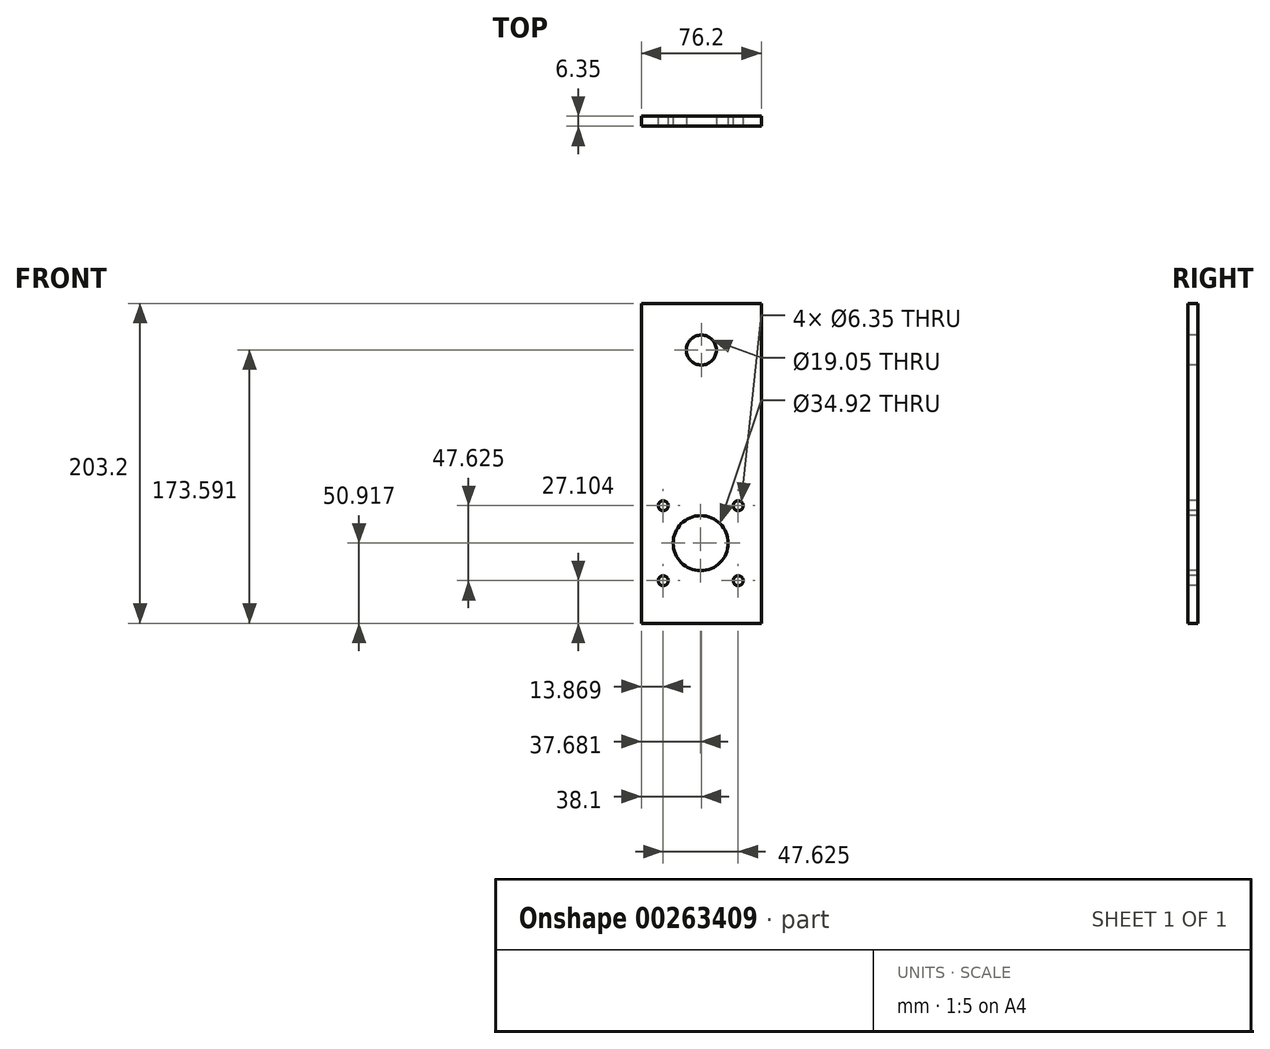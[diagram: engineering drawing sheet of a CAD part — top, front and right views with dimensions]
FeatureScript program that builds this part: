
annotation { "Feature Type Name" : "Feature", "Feature Type Description" : "" }
export const myFeature = defineFeature(function(context is Context, id is Id, definition is map)
    precondition{}
    {
        {
            var Q0;
            Q0=qCreatedBy(makeId("Front.planeOp"),FACE);
            var sketch = newSketch(context, id + "F0", { "sketchPlane" : qUnion([Q0])});
            skLineSegment(sketch, "E0.bottom", {"start": v(0, 0) * mm, "end": v(76.2, 0) * mm});
            skLineSegment(sketch, "E0.top", {"start": v(0, 203.2) * mm, "end": v(76.2, 203.2) * mm});
            skLineSegment(sketch, "E0.left", {"start": v(0, 0) * mm, "end": v(0, 203.2) * mm});
            skLineSegment(sketch, "E0.right", {"start": v(76.2, 0) * mm, "end": v(76.2, 203.2) * mm});
            skSolve(sketch);
        }
        {
            var Q0;
            Q0 = qSketchRegion(id + "F0", true);
            extrude(context, id + "F1", {"entities" : qUnion([Q0]), "depth" : 6.35 * mm});
        }
        {
            var Q0;
            Q0=makeQuery(id+"F1.opExtrude","CAP_FACE",FACE,{"disambiguationData":[OSD([sQuery(id+"F0.wireOp",EDGE,"E0.bottom"),sQuery(id+"F0.wireOp",EDGE,"E0.top"),sQuery(id+"F0.wireOp",EDGE,"E0.left"),sQuery(id+"F0.wireOp",EDGE,"E0.right")])],"isStart":false});
            var sketch = newSketch(context, id + "F2", { "sketchPlane" : qUnion([Q0])});
            skPoint(sketch, "E1", {"position": v(38.1, 176.74) * mm});
            skPoint(sketch, "E1.positionSnap0", {"position": v(38.1, 203.2) * mm});
            skPoint(sketch, "E2", {"position": v(13.87, 74.73) * mm});
            skPoint(sketch, "E3", {"position": v(61.5, 74.73) * mm});
            skPoint(sketch, "E4", {"position": v(61.5, 27.1) * mm});
            skPoint(sketch, "E5", {"position": v(13.87, 27.1) * mm});
            skLineSegment(sketch, "E6", {"start": v(13.87, 27.1) * mm, "end": v(61.5, 74.73) * mm});
            skPoint(sketch, "E7", {"position": v(37.68, 50.92) * mm});
            skSolve(sketch);
        }
        {
            var Q0;
            Q0=sQuery(id+"F2.wireOp",VERTEX,"E2");
            var Q1;
            Q1=sQuery(id+"F2.wireOp",VERTEX,"E3");
            var Q2;
            Q2=sQuery(id+"F2.wireOp",VERTEX,"E4");
            var Q3;
            Q3=sQuery(id+"F2.wireOp",VERTEX,"E5");
            var Q4;
            Q4=makeQuery(id+"F1.opExtrude","SWEPT_BODY",BODY,{"disambiguationData":[OSD([sQuery(id+"F0.wireOp",EDGE,"E0.bottom"),sQuery(id+"F0.wireOp",EDGE,"E0.top"),sQuery(id+"F0.wireOp",EDGE,"E0.left"),sQuery(id+"F0.wireOp",EDGE,"E0.right")])]});
            hole(context, id + "F3", {"style" : HoleStyle.SIMPLE, "endStyle" : HoleEndStyle.THROUGH, "holeDiameter" : 6.35 * mm, "tappedDepth" : 12.7 * mm, "tapClearance" : 3, "startFromSketch" : true, "locations" : qUnion([Q0, Q1, Q2, Q3]), "scope" : qUnion([Q4])});
        }
        {
            var Q0;
            Q0=makeQuery(id+"F1.opExtrude","CAP_FACE",FACE,{"disambiguationData":[OSD([sQuery(id+"F0.wireOp",EDGE,"E0.bottom"),sQuery(id+"F0.wireOp",EDGE,"E0.top"),sQuery(id+"F0.wireOp",EDGE,"E0.left"),sQuery(id+"F0.wireOp",EDGE,"E0.right")])],"isStart":false});
            var sketch = newSketch(context, id + "F4", { "sketchPlane" : qUnion([Q0])});
            skPoint(sketch, "E8", {"position": v(38.1, 173.6) * mm});
            skPoint(sketch, "E8.positionSnap0", {"position": v(38.1, 203.2) * mm});
            skLineSegment(sketch, "E9", {"start": v(13.87, 27.1) * mm, "end": v(61.5, 74.73) * mm});
            skPoint(sketch, "E10", {"position": v(37.68, 50.92) * mm});
            skSolve(sketch);
        }
        {
            var Q0;
            Q0=sQuery(id+"F4.wireOp",VERTEX,"E8");
            var Q1;
            Q1=makeQuery(id+"F1.opExtrude","SWEPT_BODY",BODY,{"disambiguationData":[OSD([sQuery(id+"F0.wireOp",EDGE,"E0.bottom"),sQuery(id+"F0.wireOp",EDGE,"E0.top"),sQuery(id+"F0.wireOp",EDGE,"E0.left"),sQuery(id+"F0.wireOp",EDGE,"E0.right")])]});
            hole(context, id + "F5", {"style" : HoleStyle.SIMPLE, "endStyle" : HoleEndStyle.THROUGH, "holeDiameter" : 19.05 * mm, "tappedDepth" : 12.7 * mm, "tapClearance" : 3, "startFromSketch" : true, "locations" : qUnion([Q0]), "scope" : qUnion([Q1])});
        }
        {
            var Q0;
            Q0=makeQuery(id+"F1.opExtrude","CAP_FACE",FACE,{"disambiguationData":[OSD([sQuery(id+"F0.wireOp",EDGE,"E0.bottom"),sQuery(id+"F0.wireOp",EDGE,"E0.top"),sQuery(id+"F0.wireOp",EDGE,"E0.left"),sQuery(id+"F0.wireOp",EDGE,"E0.right")])],"isStart":false});
            var sketch = newSketch(context, id + "F6", { "sketchPlane" : qUnion([Q0])});
            skLineSegment(sketch, "E11", {"start": v(13.87, 27.1) * mm, "end": v(61.5, 74.73) * mm});
            skPoint(sketch, "E12", {"position": v(37.68, 50.92) * mm});
            skSolve(sketch);
        }
        {
            var Q0;
            Q0=sQuery(id+"F6.wireOp",VERTEX,"E12");
            var Q1;
            Q1=makeQuery(id+"F1.opExtrude","SWEPT_BODY",BODY,{"disambiguationData":[OSD([sQuery(id+"F0.wireOp",EDGE,"E0.bottom"),sQuery(id+"F0.wireOp",EDGE,"E0.top"),sQuery(id+"F0.wireOp",EDGE,"E0.left"),sQuery(id+"F0.wireOp",EDGE,"E0.right")])]});
            hole(context, id + "F7", {"style" : HoleStyle.SIMPLE, "endStyle" : HoleEndStyle.THROUGH, "holeDiameter" : 34.92 * mm, "tappedDepth" : 12.7 * mm, "tapClearance" : 3, "startFromSketch" : true, "locations" : qUnion([Q0]), "scope" : qUnion([Q1])});
        }
    });
